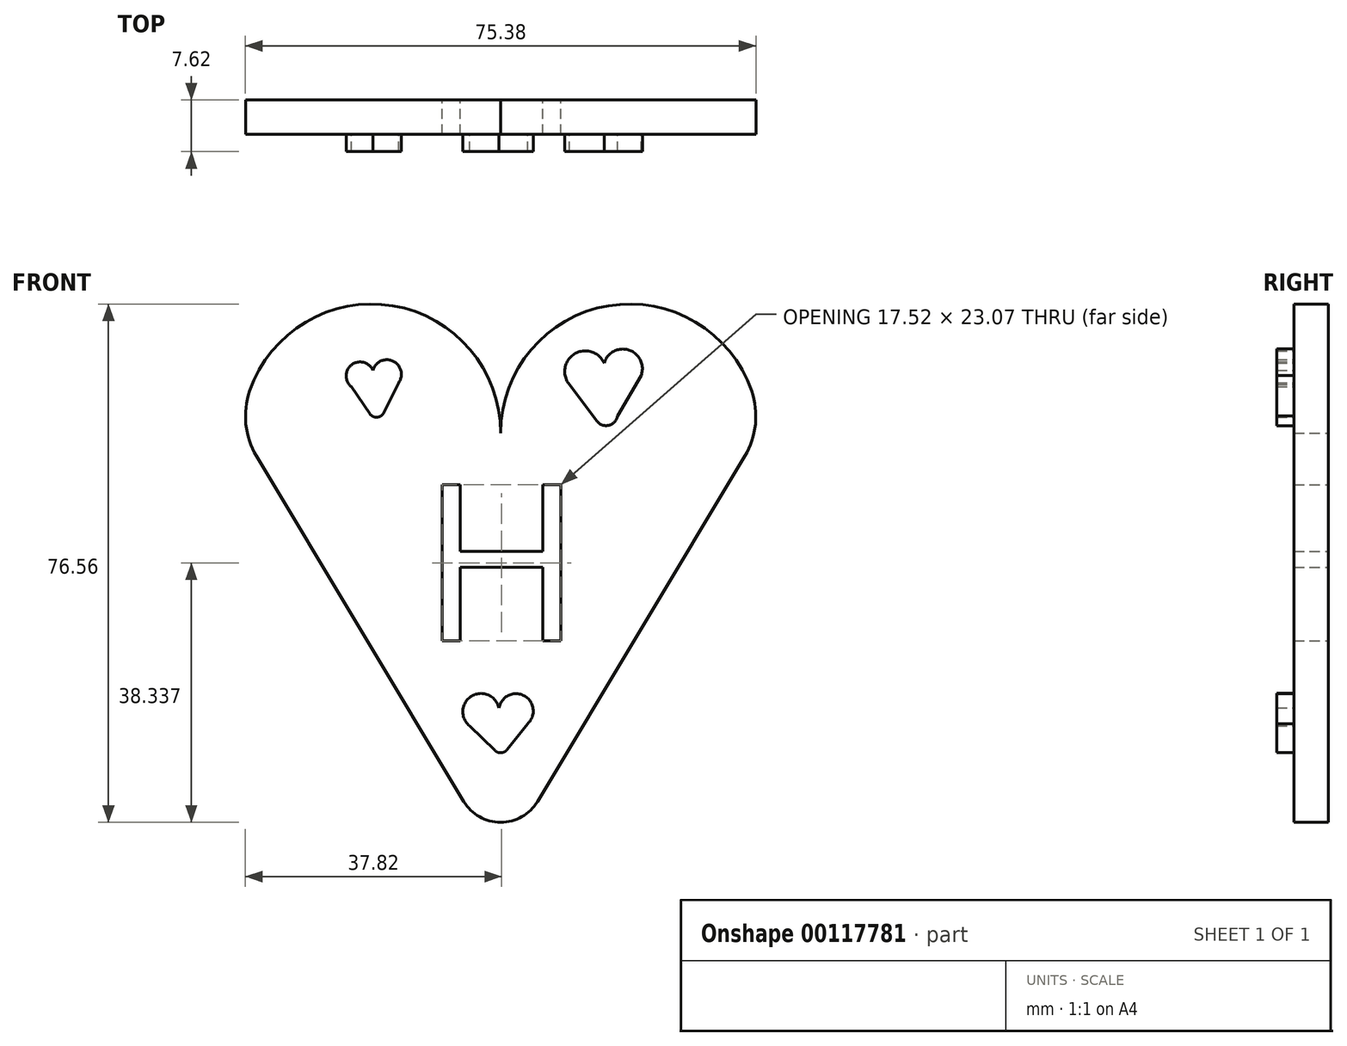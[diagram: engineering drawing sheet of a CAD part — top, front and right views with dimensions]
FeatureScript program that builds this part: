
annotation { "Feature Type Name" : "Feature", "Feature Type Description" : "" }
export const myFeature = defineFeature(function(context is Context, id is Id, definition is map)
    precondition{}
    {
        {
            var Q0;
            Q0=qCreatedBy(makeId("Front.planeOp"),FACE);
            var sketch = newSketch(context, id + "F0", { "sketchPlane" : qUnion([Q0])});
            skArc(sketch, "E0", {"start": v(37.07, 6.2) * mm, "mid": v(15.91, 18.79) * mm, "end": v(0, 0) * mm});
            skArc(sketch, "E1", {"start": v(0, 0) * mm, "mid": v(-15.91, 18.79) * mm, "end": v(-37.07, 6.2) * mm});
            skPoint(sketch, "E2", {"position": v(0, -63.5) * mm});
            skLineSegment(sketch, "E3", {"start": v(36.06, -3.4) * mm, "end": v(5.45, -54.42) * mm});
            skLineSegment(sketch, "E4", {"start": v(-36.06, -3.4) * mm, "end": v(-5.45, -54.42) * mm});
            skPoint(sketch, "E5.visualSharp", {"position": v(-38.1, 0) * mm});
            skArc(sketch, "E5.filletArc", {"start": v(-37.07, 6.2) * mm, "mid": v(-37.62, 1.28) * mm, "end": v(-36.06, -3.4) * mm});
            skPoint(sketch, "E6.visualSharp", {"position": v(38.1, 0) * mm});
            skArc(sketch, "E6.filletArc", {"start": v(36.06, -3.4) * mm, "mid": v(37.62, 1.28) * mm, "end": v(37.07, 6.2) * mm});
            skArc(sketch, "E7.filletArc", {"start": v(-5.45, -54.42) * mm, "mid": v(0, -57.5) * mm, "end": v(5.45, -54.42) * mm});
            skText(sketch, "E8", { "text": "H", "fontName": "OpenSans-Regular.ttf"});
            const initialGuessF0  = {"E8": [-0.0118, -0.03071, 1, 0, 0.02327]};
            skSetInitialGuess(sketch, initialGuessF0);
            skSolve(sketch);
        }
        {
            var Q0;
            Q0=makeQuery(id+"F0.imprint","IMPRINT",FACE,{"disambiguationData":[TD([[makeQuery(id+"F0.imprint","IMPRINT",EDGE,{"derivedFrom":sQuery(id+"F0.wireOp",EDGE,"E0")}),1.0]])]});
            extrude(context, id + "F1", {"entities" : qUnion([Q0]), "depth" : 5.08 * mm});
        }
        {
            var Q0;
            Q0=makeQuery(id+"F1.opExtrude","CAP_FACE",FACE,{"disambiguationData":[OSD([sQuery(id+"F0.wireOp",EDGE,"E0"),sQuery(id+"F0.wireOp",EDGE,"E1"),sQuery(id+"F0.wireOp",EDGE,"E3"),sQuery(id+"F0.wireOp",EDGE,"E4"),sQuery(id+"F0.wireOp",EDGE,"E5.filletArc"),sQuery(id+"F0.wireOp",EDGE,"E6.filletArc"),sQuery(id+"F0.wireOp",EDGE,"E7.filletArc"),sQuery(id+"F0.wireOp",EDGE,"E8.sketch_text.stroke-0"),sQuery(id+"F0.wireOp",EDGE,"E8.sketch_text.stroke-1"),sQuery(id+"F0.wireOp",EDGE,"E8.sketch_text.stroke-2"),sQuery(id+"F0.wireOp",EDGE,"E8.sketch_text.stroke-3"),sQuery(id+"F0.wireOp",EDGE,"E8.sketch_text.stroke-4"),sQuery(id+"F0.wireOp",EDGE,"E8.sketch_text.stroke-5"),sQuery(id+"F0.wireOp",EDGE,"E8.sketch_text.stroke-6"),sQuery(id+"F0.wireOp",EDGE,"E8.sketch_text.stroke-7"),sQuery(id+"F0.wireOp",EDGE,"E8.sketch_text.stroke-8"),sQuery(id+"F0.wireOp",EDGE,"E8.sketch_text.stroke-9"),sQuery(id+"F0.wireOp",EDGE,"E8.sketch_text.stroke-10"),sQuery(id+"F0.wireOp",EDGE,"E8.sketch_text.stroke-11")])],"isStart":false});
            var sketch = newSketch(context, id + "F2", { "sketchPlane" : qUnion([Q0])});
            skArc(sketch, "E9", {"start": v(-0.26, -40.62) * mm, "mid": v(-4.3, -38.86) * mm, "end": v(-4.58, -43.25) * mm});
            skArc(sketch, "E10", {"start": v(4.01, -42.92) * mm, "mid": v(3.47, -38.81) * mm, "end": v(-0.26, -40.62) * mm});
            skArc(sketch, "E11", {"start": v(-0.84, -46.89) * mm, "mid": v(0.08, -47.23) * mm, "end": v(0.95, -46.77) * mm});
            skArc(sketch, "E12", {"start": v(-18.87, 9.26) * mm, "mid": v(-22, 10.07) * mm, "end": v(-22.03, 6.83) * mm});
            skPoint(sketch, "E12.centerSnap0", {"position": v(-20.75, -28.91) * mm});
            skArc(sketch, "E13", {"start": v(-15.05, 7.44) * mm, "mid": v(-15.88, 10.61) * mm, "end": v(-18.87, 9.26) * mm});
            skArc(sketch, "E14", {"start": v(-19.34, 2.85) * mm, "mid": v(-18.26, 2.33) * mm, "end": v(-17.27, 2.99) * mm});
            skArc(sketch, "E15", {"start": v(15.27, 10.33) * mm, "mid": v(10.89, 11.68) * mm, "end": v(10.18, 7.14) * mm});
            skArc(sketch, "E16", {"start": v(20.75, 8.51) * mm, "mid": v(18.95, 12.25) * mm, "end": v(15.27, 10.33) * mm});
            skArc(sketch, "E17", {"start": v(14.23, 1.76) * mm, "mid": v(15.98, 1.13) * mm, "end": v(17.24, 2.5) * mm});
            skLineSegment(sketch, "E18", {"start": v(20.75, 8.51) * mm, "end": v(17.24, 2.5) * mm});
            skLineSegment(sketch, "E19", {"start": v(10.18, 7.14) * mm, "end": v(14.23, 1.76) * mm});
            skLineSegment(sketch, "E20", {"start": v(-22.03, 6.83) * mm, "end": v(-19.34, 2.85) * mm});
            skLineSegment(sketch, "E21", {"start": v(-15.05, 7.44) * mm, "end": v(-17.27, 2.99) * mm});
            skLineSegment(sketch, "E22", {"start": v(4.01, -42.92) * mm, "end": v(0.95, -46.77) * mm});
            skLineSegment(sketch, "E23", {"start": v(-4.58, -43.25) * mm, "end": v(-0.84, -46.89) * mm});
            skSolve(sketch);
        }
        {
            var Q0;
            Q0=makeQuery(id+"F2.imprint","IMPRINT",FACE,{"disambiguationData":[TD([[makeQuery(id+"F2.imprint","IMPRINT",EDGE,{"derivedFrom":sQuery(id+"F2.wireOp",EDGE,"E9")}),1.0]])]});
            var Q1;
            Q1=makeQuery(id+"F2.imprint","IMPRINT",FACE,{"disambiguationData":[TD([[makeQuery(id+"F2.imprint","IMPRINT",EDGE,{"derivedFrom":sQuery(id+"F2.wireOp",EDGE,"E15")}),1.0]])]});
            var Q2;
            Q2=makeQuery(id+"F2.imprint","IMPRINT",FACE,{"disambiguationData":[TD([[makeQuery(id+"F2.imprint","IMPRINT",EDGE,{"derivedFrom":sQuery(id+"F2.wireOp",EDGE,"E12")}),1.0]])]});
            extrude(context, id + "F3", {"entities" : qUnion([Q0, Q1, Q2]), "operationType" : NewBodyOperationType.ADD, "depth" : 2.54 * mm});
        }
    });
